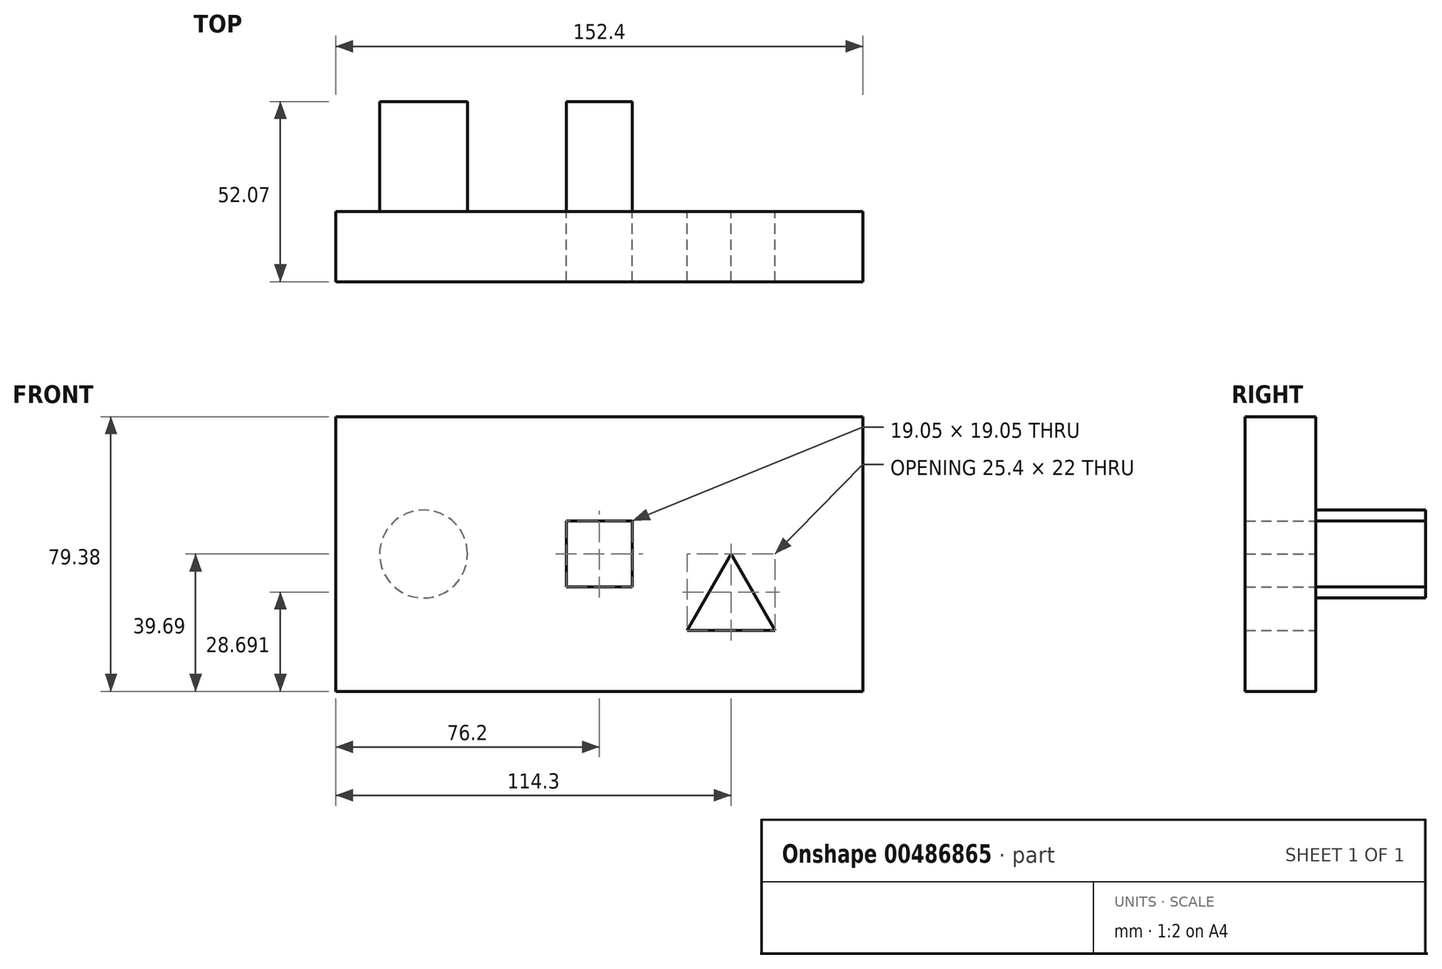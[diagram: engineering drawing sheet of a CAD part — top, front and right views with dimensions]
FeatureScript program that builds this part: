
annotation { "Feature Type Name" : "Feature", "Feature Type Description" : "" }
export const myFeature = defineFeature(function(context is Context, id is Id, definition is map)
    precondition{}
    {
        {
            var Q0;
            Q0=qCreatedBy(makeId("Front.planeOp"),FACE);
            var sketch = newSketch(context, id + "F0", { "sketchPlane" : qUnion([Q0])});
            skLineSegment(sketch, "E0", {"start": v(0, 0) * mm, "end": v(44.45, 0) * mm});
            skLineSegment(sketch, "E1", {"start": v(44.45, 39.69) * mm, "end": v(44.45, -39.69) * mm});
            skLineSegment(sketch, "E2.bottom", {"start": v(44.45, -39.69) * mm, "end": v(-107.95, -39.69) * mm});
            skLineSegment(sketch, "E2.top", {"start": v(44.45, 39.69) * mm, "end": v(-107.95, 39.69) * mm});
            skLineSegment(sketch, "E2.left", {"start": v(44.45, -39.69) * mm, "end": v(44.45, 39.69) * mm});
            skLineSegment(sketch, "E2.right", {"start": v(-107.95, -39.69) * mm, "end": v(-107.95, 39.69) * mm});
            skLineSegment(sketch, "E3", {"start": v(0, 0) * mm, "end": v(6.35, 0) * mm});
            skLineSegment(sketch, "E4", {"start": v(0, 0) * mm, "end": v(-31.75, 0) * mm});
            skLineSegment(sketch, "E5.bottom", {"start": v(-41.27, 9.52) * mm, "end": v(-22.23, 9.52) * mm});
            skLineSegment(sketch, "E5.top", {"start": v(-41.27, -9.53) * mm, "end": v(-22.23, -9.53) * mm});
            skLineSegment(sketch, "E5.left", {"start": v(-41.27, 9.52) * mm, "end": v(-41.27, -9.53) * mm});
            skLineSegment(sketch, "E5.right", {"start": v(-22.23, 9.52) * mm, "end": v(-22.23, -9.53) * mm});
            skPoint(sketch, "E5.middle", {"position": v(-31.75, 0) * mm});
            skCircle(sketch, "E6", {"center": v(-82.55, 0) * mm, "radius": 12.7 * mm});
            skLineSegment(sketch, "E7.0", {"start": v(6.35, 0) * mm, "end": v(19.05, -22) * mm});
            skLineSegment(sketch, "E7.1", {"start": v(19.05, -22) * mm, "end": v(-6.35, -22) * mm});
            skLineSegment(sketch, "E7.2", {"start": v(-6.35, -22) * mm, "end": v(6.35, 0) * mm});
            skSolve(sketch);
        }
        {
            var Q0;
            {var subQ4=sQuery(id+"F0.wireOp",EDGE,"E2.bottom");Q0=makeQuery(id+"F0.imprint","IMPRINT",FACE,{"disambiguationData":[TD([[makeQuery(id+"F0.imprint","IMPRINT",EDGE,{"derivedFrom":subQ4}),-1.0]])]});}
            extrude(context, id + "F1", {"entities" : qUnion([Q0]), "depth" : 20.32 * mm});
        }
        {
            var Q0;
            Q0=makeQuery(id+"F0.imprint","IMPRINT",FACE,{"disambiguationData":[TD([[makeQuery(id+"F0.imprint","IMPRINT",EDGE,{"derivedFrom":sQuery(id+"F0.wireOp",EDGE,"E6")}),1.0]])]});
            extrude(context, id + "F2", {"entities" : qUnion([Q0]), "operationType" : NewBodyOperationType.ADD, "depth" : 20.32 * mm});
        }
        {
            var Q0;
            Q0=makeQuery(id+"F0.imprint","IMPRINT",FACE,{"disambiguationData":[TD([[makeQuery(id+"F0.imprint","IMPRINT",EDGE,{"derivedFrom":sQuery(id+"F0.wireOp",EDGE,"E6")}),1.0]])]});
            extrude(context, id + "F3", {"entities" : qUnion([Q0]), "operationType" : NewBodyOperationType.ADD, "oppositeDirection" : true, "depth" : 31.75 * mm});
        }
        {
            var Q0;
            {var subQ1=sQuery(id+"F0.wireOp",EDGE,"E5.bottom");Q0=makeQuery(id+"F0.imprint","IMPRINT",FACE,{"disambiguationData":[TD([[makeQuery(id+"F0.imprint","IMPRINT",EDGE,{"derivedFrom":subQ1}),-1.0]])]});}
            extrude(context, id + "F4", {"entities" : qUnion([Q0]), "operationType" : NewBodyOperationType.ADD, "oppositeDirection" : true, "depth" : 31.75 * mm});
        }
    });
